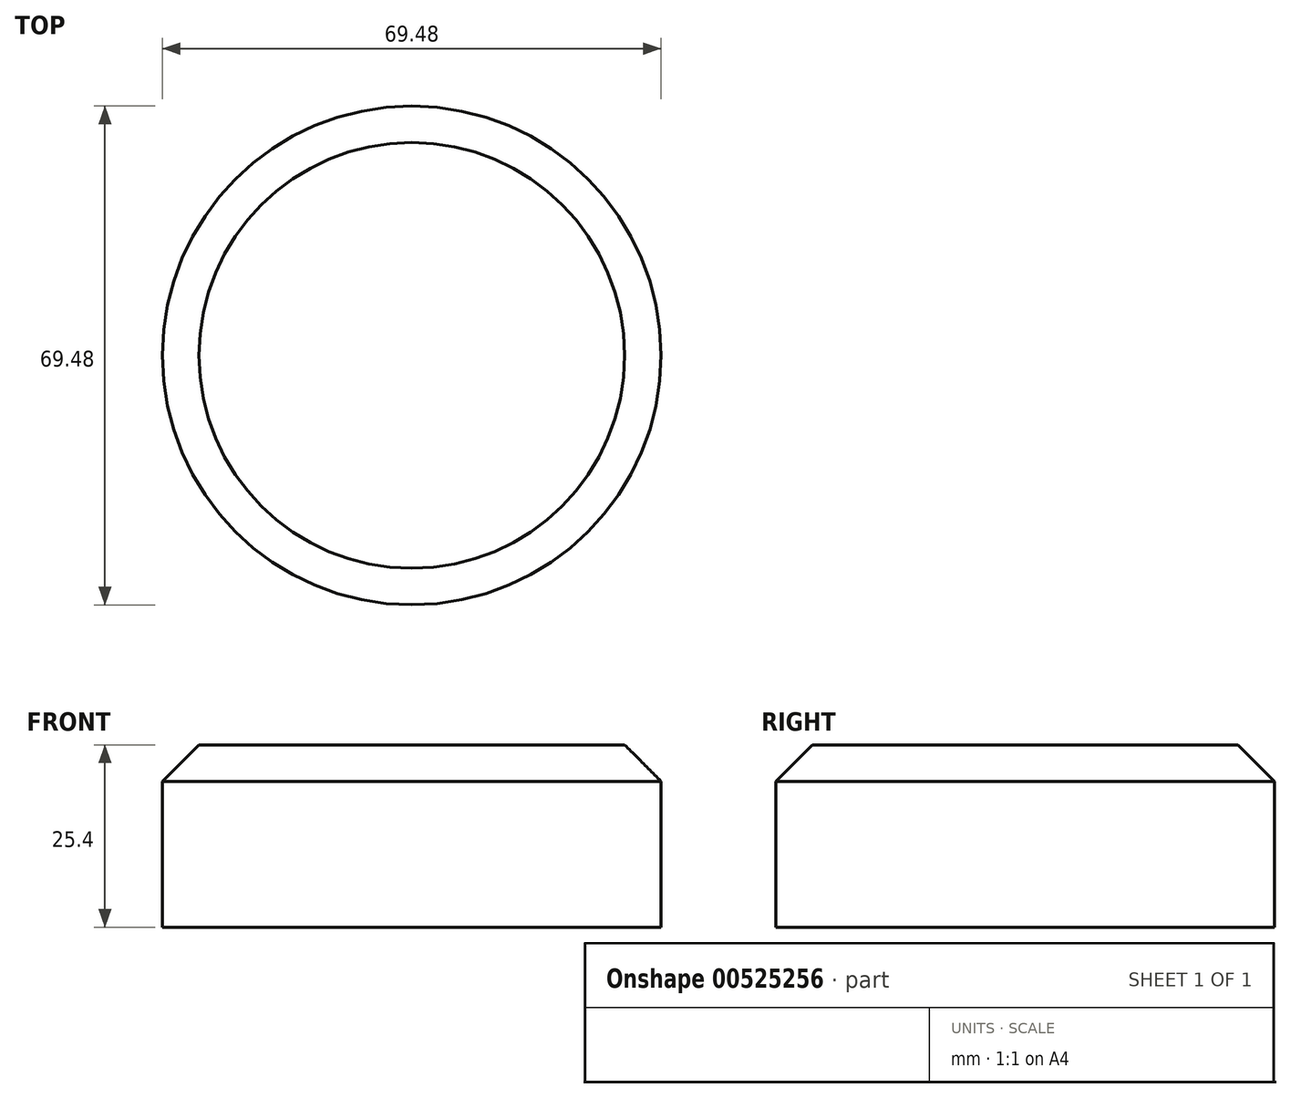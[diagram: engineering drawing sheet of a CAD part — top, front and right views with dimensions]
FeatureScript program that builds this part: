
annotation { "Feature Type Name" : "Feature", "Feature Type Description" : "" }
export const myFeature = defineFeature(function(context is Context, id is Id, definition is map)
    precondition{}
    {
        {
            var Q0;
            Q0=qCreatedBy(makeId("Top.planeOp"),FACE);
            var sketch = newSketch(context, id + "F0", { "sketchPlane" : qUnion([Q0])});
            skCircle(sketch, "E0", {"center": v(0, 0) * mm, "radius": 34.74 * mm});
            skSolve(sketch);
        }
        {
            var Q0;
            Q0 = qSketchRegion(id + "F0", true);
            extrude(context, id + "F1", {"entities" : qUnion([Q0]), "depth" : 25.4 * mm, "offsetDistance" : 25.4 * mm});
        }
        {
            var Q0;
            Q0=makeQuery(id+"F1.opExtrude","CAP_EDGE",EDGE,{"disambiguationData":[OSD([sQuery(id+"F0.wireOp",EDGE,"E0")])],"isStart":false});
            chamfer(context, id + "F2", {"entities" : qUnion([Q0]), "width" : 5.08 * mm, "tangentPropagation" : true});
        }
    });
